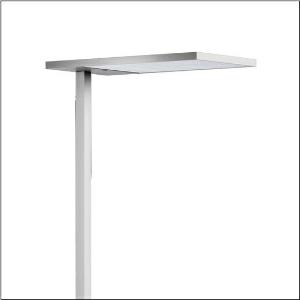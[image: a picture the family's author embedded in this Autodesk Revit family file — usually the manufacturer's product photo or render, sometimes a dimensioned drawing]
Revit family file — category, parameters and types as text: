
# Revit family: silica_21_floor_r_51mx53sg4es
name_source: partatom
category: Lighting Fixtures
units: mm (PartAtom-declared; Revit-internal decimal feet)

## family parameters
Cut with Voids When Loaded = No
Host = Face
Light Source = No
Part Type = Normal
Room Calculation Point = No
Round Connector Dimension = Use Diameter
Shared = No

## types (1)
- Silica 21 Floor R (1 x LED, 15000 lm, 106.4 W, 4000K)
    Apparent Load = 106 VA
    CIE Flux Codes = 54 86 97 13 100
    Color Rendering = 80
    Color Temperature = 4000K
    Default Elevation = 1800 mm
    Description = Silica® 21 Floor R, floorstanding luminaire, of PMMA, primary optical cover: prismatic diffuser, of PMMA, CAT 2 (L<= 3000cd/m²), light emission: indirect/direct distribution, primary light characteristic: symmetric, primary optical cover: cover panel, of PMMA, installation type: not mounted, LED, rated luminous flux: 15.000lm, luminous efficacy: 141lm/W, light colour: 840, colour temperature: 4000K, control gear: DALI 2, daylight-dependent control, mains connection: 230V, AC, 50/60Hz, connection cable included, cable length: 2,5m, rated input power: 106.4W, luminaire head, of aluminium, powder-coated, metallic grey (RAL 9006), length: 671mm, width: 371mm, height: 2010mm, supporting column, angular, of aluminium, powder-coated, metallic grey (RAL 9006), baseplate, of steel, powder-coated, metallic grey (RAL 9006), sensor module PR3-S, local control - self-sufficient standalone sensors, equipment: master, direct and indirect component separately switchable, protection rating (complete): IP20, insulation class (complete): insulation class I (protective earthing), certification: CE, permissible operating ambient temperature: 0..+35°C, standard: EN 50419, packaging unit: 1 piece
    Height = 18 mm
    Lamp = 1 x LED
    Lamp Light Flux = 15000 lm
    Lamp Power = 106.4 W
    Lamp count = 1
    Length = 650 mm
    Luminous efficacy = 141 lm/W
    Manufacturer = Siteco
    ModVariant = No
    Model = 51MX53SG4ES
    Mounting Place = Floor
    Mounting Type = Freestanding
    Number of Poles = 1
    OnlyDefault = Yes
    Power Factor = 1
    Product Name = Silica 21 Floor R
    Product group = floorstanding luminaire
    ProductGroupID = 1302
    Protection Class = Protection class I
    Protection Degree = IP 20
    RLX_Detail_Level = 1
    RLX_Emergency_Light_Flux = 0 lm
    RLX_Emergency_Type = 0
    RLX_Emergency_Type_DB = No
    RlxData = <blob elided: 20537 chars, md5=260a9917>
    Socket = socket
    Standby Power = 0 W
    System Light Flux = 15000 lm
    System Power = 106 W
    Type Comments = Product without accessories
    Type Image = l_1006716.jpg
    URL = http://relux.com
    VarID = ---
    Voltage = 0 V
    Weight = 0.00 kg
    Width = 350 mm

## geometry (parser evidence)
native form markers: Blend x4, Sweep x17
no freeform markers — native parametric forms only
